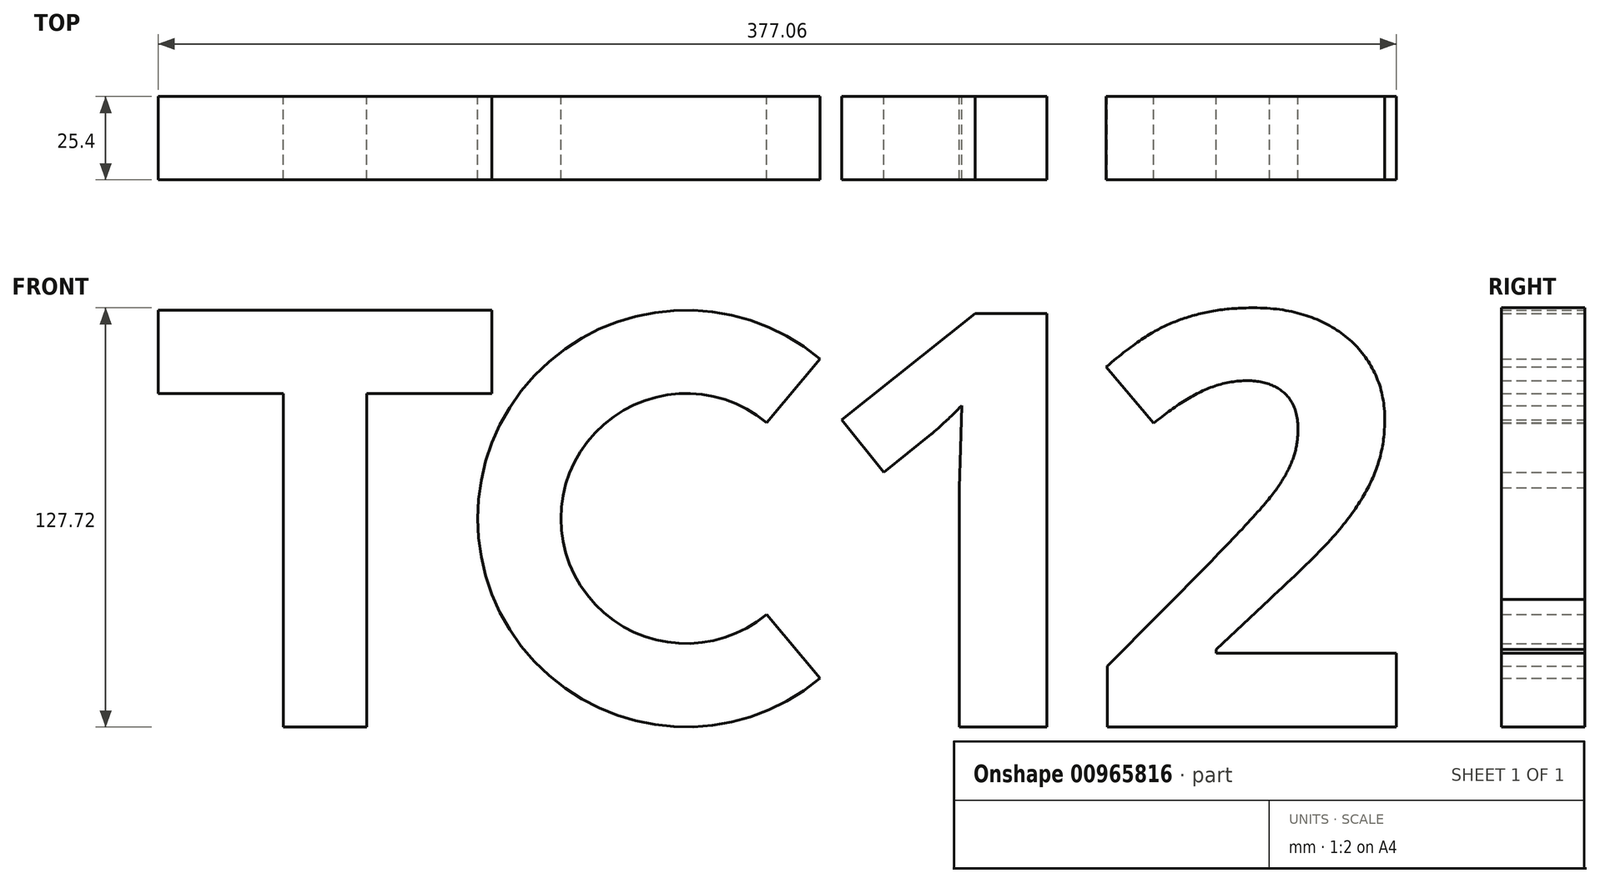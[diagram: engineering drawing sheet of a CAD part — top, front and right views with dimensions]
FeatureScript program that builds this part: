
annotation { "Feature Type Name" : "Feature", "Feature Type Description" : "" }
export const myFeature = defineFeature(function(context is Context, id is Id, definition is map)
    precondition{}
    {
        {
            var Q0;
            Q0=qCreatedBy(makeId("Front.planeOp"),FACE);
            var sketch = newSketch(context, id + "F0", { "sketchPlane" : qUnion([Q0])});
            skLineSegment(sketch, "E0", {"start": v(-40.6, -23.06) * mm, "end": v(35.6, -23.06) * mm});
            skLineSegment(sketch, "E1.bottom", {"start": v(-146.88, 127) * mm, "end": v(-45.28, 127) * mm});
            skLineSegment(sketch, "E1.top", {"start": v(-146.88, 101.6) * mm, "end": v(-45.28, 101.6) * mm});
            skLineSegment(sketch, "E1.left", {"start": v(-146.88, 127) * mm, "end": v(-146.88, 101.6) * mm});
            skLineSegment(sketch, "E1.right", {"start": v(-45.28, 127) * mm, "end": v(-45.28, 101.6) * mm});
            skLineSegment(sketch, "E2.bottom", {"start": v(-108.78, 101.6) * mm, "end": v(-83.38, 101.6) * mm});
            skLineSegment(sketch, "E2.top", {"start": v(-108.78, 0) * mm, "end": v(-83.38, 0) * mm});
            skLineSegment(sketch, "E2.left", {"start": v(-108.78, 101.6) * mm, "end": v(-108.78, 0) * mm});
            skLineSegment(sketch, "E2.right", {"start": v(-83.38, 101.6) * mm, "end": v(-83.38, 0) * mm});
            skArc(sketch, "E3", {"start": v(54.72, 112.14) * mm, "mid": v(-49.6, 63.5) * mm, "end": v(54.72, 14.86) * mm});
            skArc(sketch, "E4", {"start": v(38.4, 92.69) * mm, "mid": v(-24.2, 63.5) * mm, "end": v(38.4, 34.31) * mm});
            skLineSegment(sketch, "E5", {"start": v(-96.08, 127) * mm, "end": v(-96.08, 26.7) * mm, "construction": true});
            skLineSegment(sketch, "E6", {"start": v(54.72, 112.14) * mm, "end": v(38.4, 92.69) * mm});
            skLineSegment(sketch, "E7", {"start": v(38.4, 34.31) * mm, "end": v(54.72, 14.86) * mm});
            skLineSegment(sketch, "E8", {"start": v(13.9, 127) * mm, "end": v(13.9, 0) * mm, "construction": true});
            skText(sketch, "E9", { "text": "1\n", "fontName": "OpenSans-Bold.ttf"});
            skText(sketch, "E10", { "text": "2", "fontName": "OpenSans-Bold.ttf"});
            const initialGuessF0  = {"E9": [0.0509, 0, 1, 0, 0.127], "E10": [0.1351, 0, 1, 0, 0.127]};
            skSetInitialGuess(sketch, initialGuessF0);
            skSolve(sketch);
        }
        {
            var Q0;
            Q0 = qSketchRegion(id + "F0", true);
            extrude(context, id + "F1", {"entities" : qUnion([Q0]), "depth" : 25.4 * mm, "offsetDistance" : 25.4 * mm});
        }
    });
